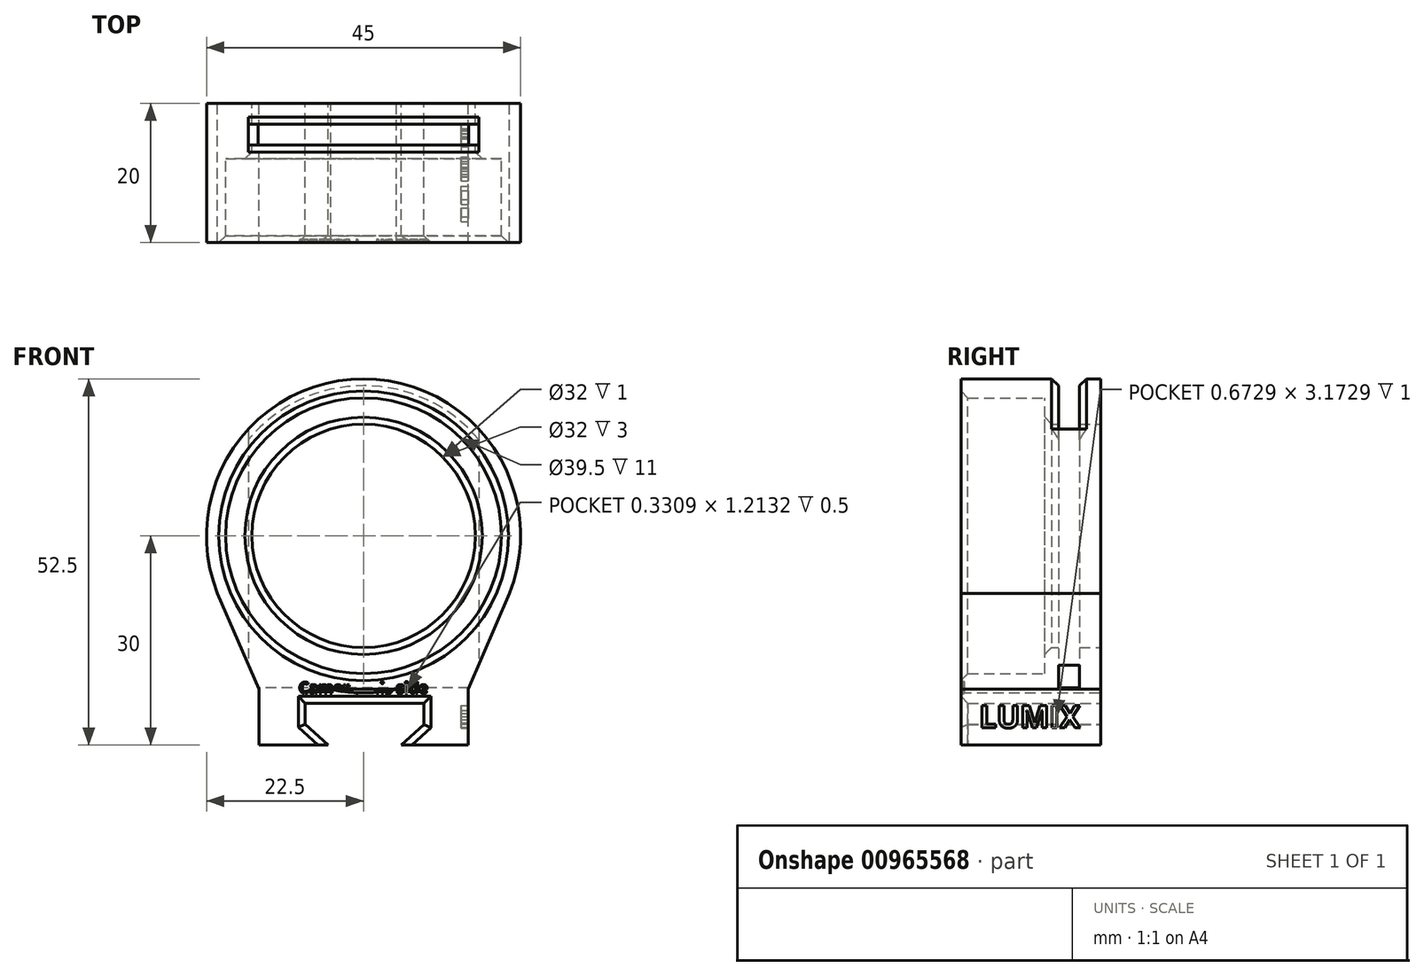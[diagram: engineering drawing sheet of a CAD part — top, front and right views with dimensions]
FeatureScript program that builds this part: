
annotation { "Feature Type Name" : "Feature", "Feature Type Description" : "" }
export const myFeature = defineFeature(function(context is Context, id is Id, definition is map)
    precondition{}
    {
        {
            var Q0;
            Q0=qCreatedBy(makeId("Front.planeOp"),FACE);
            var sketch = newSketch(context, id + "F0", { "sketchPlane" : qUnion([Q0])});
            skLineSegment(sketch, "E0.top", {"start": v(-15, -9.67) * mm, "end": v(15, -9.67) * mm});
            skLineSegment(sketch, "E0.left", {"start": v(-15, -1.67) * mm, "end": v(-15, -9.67) * mm});
            skLineSegment(sketch, "E0.right", {"start": v(15, -1.67) * mm, "end": v(15, -9.67) * mm});
            skLineSegment(sketch, "E1.bottom", {"start": v(-8.57, -3.67) * mm, "end": v(8.93, -3.67) * mm});
            skLineSegment(sketch, "E1.top", {"start": v(-8.57, -9.67) * mm, "end": v(8.93, -9.67) * mm});
            skLineSegment(sketch, "E1.left", {"start": v(-8.57, -3.67) * mm, "end": v(-8.57, -9.67) * mm});
            skLineSegment(sketch, "E1.right", {"start": v(8.93, -3.67) * mm, "end": v(8.93, -9.67) * mm});
            skLineSegment(sketch, "E2.left", {"start": v(-8.57, -9.67) * mm, "end": v(-8.57, -5.78) * mm});
            skLineSegment(sketch, "E3.left", {"start": v(8.93, -9.67) * mm, "end": v(8.93, -5.67) * mm});
            skPoint(sketch, "E4", {"position": v(-8.57, -6.67) * mm});
            skLineSegment(sketch, "E5.bottom", {"start": v(-8.57, -9.67) * mm, "end": v(-9.71, -9.67) * mm, "construction": true});
            skLineSegment(sketch, "E5.top", {"start": v(-8.57, -6.47) * mm, "end": v(-9.71, -6.47) * mm, "construction": true});
            skLineSegment(sketch, "E5.left", {"start": v(-8.57, -9.67) * mm, "end": v(-8.57, -6.47) * mm, "construction": true});
            skLineSegment(sketch, "E5.right", {"start": v(-9.71, -9.67) * mm, "end": v(-9.71, -6.47) * mm, "construction": true});
            skPoint(sketch, "E6.oppositeSnap0", {"position": v(-9.14, -6.47) * mm});
            skLineSegment(sketch, "E6.bottom", {"start": v(8.93, -9.67) * mm, "end": v(10.57, -9.67) * mm, "construction": true});
            skLineSegment(sketch, "E6.top", {"start": v(8.93, -6.47) * mm, "end": v(10.57, -6.47) * mm, "construction": true});
            skLineSegment(sketch, "E6.left", {"start": v(8.93, -9.67) * mm, "end": v(8.93, -6.47) * mm, "construction": true});
            skLineSegment(sketch, "E6.right", {"start": v(10.57, -9.67) * mm, "end": v(10.57, -6.47) * mm, "construction": true});
            skLineSegment(sketch, "E7.bottom", {"start": v(-8.57, -9.67) * mm, "end": v(-5.07, -9.67) * mm, "construction": true});
            skLineSegment(sketch, "E7.top", {"start": v(-8.57, -11.6) * mm, "end": v(-5.07, -11.6) * mm, "construction": true});
            skLineSegment(sketch, "E7.left", {"start": v(-8.57, -9.67) * mm, "end": v(-8.57, -11.6) * mm, "construction": true});
            skLineSegment(sketch, "E7.right", {"start": v(-5.07, -9.67) * mm, "end": v(-5.07, -11.6) * mm, "construction": true});
            skLineSegment(sketch, "E8.bottom", {"start": v(8.93, -9.67) * mm, "end": v(5.43, -9.67) * mm, "construction": true});
            skLineSegment(sketch, "E8.top", {"start": v(8.93, -11.48) * mm, "end": v(5.43, -11.48) * mm, "construction": true});
            skLineSegment(sketch, "E8.left", {"start": v(8.93, -9.67) * mm, "end": v(8.93, -11.48) * mm, "construction": true});
            skLineSegment(sketch, "E8.right", {"start": v(5.43, -9.67) * mm, "end": v(5.43, -11.48) * mm, "construction": true});
            skLineSegment(sketch, "E9", {"start": v(-8.57, -6.47) * mm, "end": v(-5.07, -9.67) * mm});
            skLineSegment(sketch, "E10", {"start": v(5.43, -9.67) * mm, "end": v(8.93, -6.47) * mm});
            skLineSegment(sketch, "E11", {"start": v(-15, -1.67) * mm, "end": v(15, -1.67) * mm});
            skLineSegment(sketch, "E12", {"start": v(0, -1.67) * mm, "end": v(0, 20.33) * mm, "construction": true});
            skCircle(sketch, "E13", {"center": v(0, 20.33) * mm, "radius": 19.75 * mm});
            skCircle(sketch, "E14", {"center": v(0, 20.33) * mm, "radius": 22.5 * mm});
            skLineSegment(sketch, "E15", {"start": v(15, -1.67) * mm, "end": v(20.92, 12.05) * mm});
            skLineSegment(sketch, "E16", {"start": v(-15, -1.67) * mm, "end": v(-20.92, 12.05) * mm});
            skLineSegment(sketch, "E17", {"start": v(15, -4.92) * mm, "end": v(0, -4.92) * mm, "construction": true});
            skLineSegment(sketch, "E18", {"start": v(-15, -4.53) * mm, "end": v(0, -4.53) * mm, "construction": true});
            skLineSegment(sketch, "E19", {"start": v(-8.35, -3.67) * mm, "end": v(-8.35, -6.67) * mm});
            skLineSegment(sketch, "E20", {"start": v(8.67, -3.67) * mm, "end": v(8.67, -6.7) * mm});
            skCircle(sketch, "E21", {"center": v(0, 20.33) * mm, "radius": 16 * mm});
            skSolve(sketch);
        }
        {
            var Q0;
            {var subQ7=sQuery(id+"F0.wireOp",EDGE,"E0.left");Q0=makeQuery(id+"F0.imprint","IMPRINT",FACE,{"disambiguationData":[TD([[makeQuery(id+"F0.imprint","IMPRINT",EDGE,{"derivedFrom":subQ7}),1.0]])]});}
            var Q1;
            {var subQ3=sQuery(id+"F0.wireOp",EDGE,"E9");Q1=makeQuery(id+"F0.imprint","IMPRINT",FACE,{"disambiguationData":[TD([[makeQuery(id+"F0.imprint","IMPRINT",EDGE,{"derivedFrom":subQ3}),-1.0]])]});}
            var Q2;
            {var subQ3=sQuery(id+"F0.wireOp",EDGE,"E10");Q2=makeQuery(id+"F0.imprint","IMPRINT",FACE,{"disambiguationData":[TD([[makeQuery(id+"F0.imprint","IMPRINT",EDGE,{"derivedFrom":subQ3}),-1.0]])]});}
            var Q3;
            Q3=makeQuery(id+"F0.imprint","IMPRINT",FACE,{"disambiguationData":[TD([[makeQuery(id+"F0.imprint","IMPRINT",EDGE,{"derivedFrom":sQuery(id+"F0.wireOp",EDGE,"E13")}),-1.0]])]});
            var Q4;
            {var subQ0=sQuery(id+"F0.wireOp",EDGE,"E14");var subQ1=sQuery(id+"F0.wireOp",EDGE,"E11");var subQ2=makeQuery(id+"F0.imprint","INTERSECT",VERTEX,{"disambiguationData":[OD(0.0)],"derivedFrom":[subQ1,subQ0]});Q4=makeQuery(id+"F0.imprint","IMPRINT",FACE,{"disambiguationData":[TD([[makeQuery(id+"F0.imprint","IMPRINT",EDGE,{"disambiguationData":[TD([[subQ2,-1.0]])],"derivedFrom":subQ1}),-1.0]])]});}
            var Q5;
            {var subQ0=sQuery(id+"F0.wireOp",EDGE,"E16");var subQ3=sQuery(id+"F0.wireOp",EDGE,"E14");var subQ5=makeQuery(id+"F0.imprint","INTERSECT",VERTEX,{"disambiguationData":[OD(1.0)],"derivedFrom":[subQ3,subQ0]});Q5=makeQuery(id+"F0.imprint","IMPRINT",FACE,{"disambiguationData":[TD([[makeQuery(id+"F0.imprint","IMPRINT",EDGE,{"disambiguationData":[TD([[subQ5,-1.0]])],"derivedFrom":subQ3}),-1.0]])]});}
            var Q6;
            {var subQ0=sQuery(id+"F0.wireOp",EDGE,"E15");var subQ3=sQuery(id+"F0.wireOp",EDGE,"E14");var subQ5=makeQuery(id+"F0.imprint","INTERSECT",VERTEX,{"disambiguationData":[OD(1.0)],"derivedFrom":[subQ3,subQ0]});Q6=makeQuery(id+"F0.imprint","IMPRINT",FACE,{"disambiguationData":[TD([[makeQuery(id+"F0.imprint","IMPRINT",EDGE,{"disambiguationData":[TD([[subQ5,1.0]])],"derivedFrom":subQ3}),-1.0]])]});}
            var Q7;
            {var subQ4=sQuery(id+"F0.wireOp",EDGE,"E1.right");Q7=makeQuery(id+"F0.imprint","IMPRINT",FACE,{"disambiguationData":[TD([[makeQuery(id+"F0.imprint","IMPRINT",EDGE,{"derivedFrom":subQ4}),-1.0]])]});}
            var Q8;
            {var subQ4=sQuery(id+"F0.wireOp",EDGE,"E1.left");Q8=makeQuery(id+"F0.imprint","IMPRINT",FACE,{"disambiguationData":[TD([[makeQuery(id+"F0.imprint","IMPRINT",EDGE,{"derivedFrom":subQ4}),1.0]])]});}
            extrude(context, id + "F1", {"entities" : qUnion([Q0, Q1, Q2, Q3, Q4, Q5, Q6, Q7, Q8]), "depth" : 20 * mm, "offsetDistance" : 25 * mm});
        }
        {
            var Q0;
            Q0=qCreatedBy(makeId("Right.planeOp"),FACE);
            var sketch = newSketch(context, id + "F2", { "sketchPlane" : qUnion([Q0])});
            skLineSegment(sketch, "E22.bottom", {"start": v(0, -1.47) * mm, "end": v(-3, -1.47) * mm, "construction": true});
            skLineSegment(sketch, "E22.top", {"start": v(0, 48.53) * mm, "end": v(-3, 48.53) * mm, "construction": true});
            skLineSegment(sketch, "E22.left", {"start": v(0, -1.47) * mm, "end": v(0, 48.53) * mm, "construction": true});
            skLineSegment(sketch, "E22.right", {"start": v(-3, -1.47) * mm, "end": v(-3, 48.53) * mm, "construction": true});
            skLineSegment(sketch, "E23.bottom", {"start": v(-3, 48.53) * mm, "end": v(-6, 48.53) * mm});
            skLineSegment(sketch, "E23.top", {"start": v(-3, -1.47) * mm, "end": v(-6, -1.47) * mm});
            skLineSegment(sketch, "E23.left", {"start": v(-3, 48.53) * mm, "end": v(-3, -1.47) * mm});
            skLineSegment(sketch, "E23.right", {"start": v(-6, 48.53) * mm, "end": v(-6, -1.47) * mm});
            skSolve(sketch);
        }
        {
            var Q0;
            Q0=makeQuery(id+"F0.imprint","IMPRINT",FACE,{"disambiguationData":[TD([[makeQuery(id+"F0.imprint","IMPRINT",EDGE,{"derivedFrom":sQuery(id+"F0.wireOp",EDGE,"E13")}),1.0]])]});
            extrude(context, id + "F3", {"entities" : qUnion([Q0]), "operationType" : NewBodyOperationType.ADD, "depth" : 8 * mm, "offsetDistance" : 25 * mm});
        }
        {
            var Q0;
            Q0=makeQuery(id+"F3.opExtrude","CAP_EDGE",EDGE,{"disambiguationData":[OSD([sQuery(id+"F0.wireOp",EDGE,"E21")])],"isStart":false});
            chamfer(context, id + "F4", {"entities" : qUnion([Q0]), "width" : 1 * mm, "tangentPropagation" : true});
        }
        {
            var Q0;
            Q0=makeQuery(id+"F1.opExtrude","CAP_EDGE",EDGE,{"disambiguationData":[OSD([sQuery(id+"F0.wireOp",EDGE,"E13")])],"isStart":false});
            var Q1;
            Q1=makeQuery(id+"F1.opExtrude","CAP_EDGE",EDGE,{"disambiguationData":[OSD([sQuery(id+"F0.wireOp",EDGE,"E19")])],"isStart":false});
            var Q2;
            Q2=makeQuery(id+"F1.opExtrude","CAP_EDGE",EDGE,{"disambiguationData":[OSD([sQuery(id+"F0.wireOp",EDGE,"E1.bottom")])],"isStart":false});
            var Q3;
            Q3=makeQuery(id+"F1.opExtrude","CAP_EDGE",EDGE,{"disambiguationData":[OSD([sQuery(id+"F0.wireOp",EDGE,"E20")])],"isStart":false});
            var Q4;
            Q4=makeQuery(id+"F1.opExtrude","CAP_EDGE",EDGE,{"disambiguationData":[OSD([sQuery(id+"F0.wireOp",EDGE,"E10")])],"isStart":false});
            var Q5;
            Q5=makeQuery(id+"F1.opExtrude","CAP_EDGE",EDGE,{"disambiguationData":[OSD([sQuery(id+"F0.wireOp",EDGE,"E9")])],"isStart":false});
            chamfer(context, id + "F5", {"entities" : qUnion([Q0, Q1, Q2, Q3, Q4, Q5]), "width" : 1 * mm, "tangentPropagation" : true});
        }
        {
            var Q0;
            Q0=makeQuery(id+"F2.imprint","IMPRINT",FACE,{"disambiguationData":[TD([[makeQuery(id+"F2.imprint","IMPRINT",EDGE,{"derivedFrom":sQuery(id+"F2.wireOp",EDGE,"E23.bottom")}),1.0]])]});
            extrude(context, id + "F6", {"entities" : qUnion([Q0]), "operationType" : NewBodyOperationType.REMOVE, "depth" : 33 * mm, "offsetDistance" : 25 * mm, "symmetric" : true});
        }
        {
            var Q0;
            Q0=makeQuery(id+"F6.boolean.opBoolean","INTERSECT",EDGE,{"derivedFrom":[makeQuery(id+"F1.opExtrude","SWEPT_FACE",FACE,{"disambiguationData":[OSD([sQuery(id+"F0.wireOp",EDGE,"E14")])]}),makeQuery(id+"F6.opExtrude","SWEPT_FACE",FACE,{"disambiguationData":[OSD([sQuery(id+"F2.wireOp",EDGE,"E23.right")])]})]});
            var Q1;
            Q1=makeQuery(id+"F6.boolean.opBoolean","INTERSECT",EDGE,{"derivedFrom":[makeQuery(id+"F1.opExtrude","SWEPT_FACE",FACE,{"disambiguationData":[OSD([sQuery(id+"F0.wireOp",EDGE,"E14")])]}),makeQuery(id+"F6.opExtrude","SWEPT_FACE",FACE,{"disambiguationData":[OSD([sQuery(id+"F2.wireOp",EDGE,"E23.left")])]})]});
            chamfer(context, id + "F7", {"entities" : qUnion([Q0, Q1]), "width" : 1 * mm, "tangentPropagation" : true});
        }
        {
            var Q0;
            Q0=makeQuery(id+"F1.opExtrude","SWEPT_FACE",FACE,{"disambiguationData":[OSD([sQuery(id+"F0.wireOp",EDGE,"E0.right")])]});
            var sketch = newSketch(context, id + "F8", { "sketchPlane" : qUnion([Q0])});
            skText(sketch, "E24", { "text": "LUMIX", "fontName": "OpenSans-Bold.ttf"});
            const initialGuessF8  = {"E24": [-0.01739, -0.0072, 1, 0, 0.0032]};
            skSetInitialGuess(sketch, initialGuessF8);
            skSolve(sketch);
        }
        {
            var Q0;
            Q0=makeQuery(id+"F8.imprint","IMPRINT",FACE,{"disambiguationData":[TD([[makeQuery(id+"F8.imprint","IMPRINT",EDGE,{"derivedFrom":sQuery(id+"F8.wireOp",EDGE,"E24.sketch_text.stroke-0")}),-1.0]])]});
            var Q1;
            Q1=makeQuery(id+"F8.imprint","IMPRINT",FACE,{"disambiguationData":[TD([[makeQuery(id+"F8.imprint","IMPRINT",EDGE,{"derivedFrom":sQuery(id+"F8.wireOp",EDGE,"E24.sketch_text.stroke-6")}),-1.0]])]});
            var Q2;
            Q2=makeQuery(id+"F8.imprint","IMPRINT",FACE,{"disambiguationData":[TD([[makeQuery(id+"F8.imprint","IMPRINT",EDGE,{"derivedFrom":sQuery(id+"F8.wireOp",EDGE,"E24.sketch_text.stroke-21")}),-1.0]])]});
            var Q3;
            Q3=makeQuery(id+"F8.imprint","IMPRINT",FACE,{"disambiguationData":[TD([[makeQuery(id+"F8.imprint","IMPRINT",EDGE,{"derivedFrom":sQuery(id+"F8.wireOp",EDGE,"E24.sketch_text.stroke-40")}),-1.0]])]});
            var Q4;
            Q4=makeQuery(id+"F8.imprint","IMPRINT",FACE,{"disambiguationData":[TD([[makeQuery(id+"F8.imprint","IMPRINT",EDGE,{"derivedFrom":sQuery(id+"F8.wireOp",EDGE,"E24.sketch_text.stroke-44")}),-1.0]])]});
            extrude(context, id + "F9", {"entities" : qUnion([Q0, Q1, Q2, Q3, Q4]), "operationType" : NewBodyOperationType.REMOVE, "oppositeDirection" : true, "depth" : 1 * mm, "offsetDistance" : 25 * mm});
        }
        {
            var Q0;
            Q0=makeQuery(id+"F1.opExtrude","CAP_FACE",FACE,{"disambiguationData":[OSD([sQuery(id+"F0.wireOp",EDGE,"E0.top"),sQuery(id+"F0.wireOp",EDGE,"E0.left"),sQuery(id+"F0.wireOp",EDGE,"E0.right"),sQuery(id+"F0.wireOp",EDGE,"E1.bottom"),sQuery(id+"F0.wireOp",EDGE,"E1.top"),sQuery(id+"F0.wireOp",EDGE,"E9"),sQuery(id+"F0.wireOp",EDGE,"E10"),sQuery(id+"F0.wireOp",EDGE,"E13"),sQuery(id+"F0.wireOp",EDGE,"E14"),sQuery(id+"F0.wireOp",EDGE,"E15"),sQuery(id+"F0.wireOp",EDGE,"E16"),sQuery(id+"F0.wireOp",EDGE,"E19"),sQuery(id+"F0.wireOp",EDGE,"E20")])],"isStart":false});
            var sketch = newSketch(context, id + "F10", { "sketchPlane" : qUnion([Q0])});
            skText(sketch, "E25", { "text": "Camera this side", "fontName": "OpenSans-Bold.ttf"});
            const initialGuessF10  = {"E25": [-0.00926, -0.00223, 1, 0, 0.0016]};
            skSetInitialGuess(sketch, initialGuessF10);
            skSolve(sketch);
        }
        {
            var Q0;
            Q0=makeQuery(id+"F10.imprint","IMPRINT",FACE,{"disambiguationData":[TD([[makeQuery(id+"F10.imprint","IMPRINT",EDGE,{"derivedFrom":sQuery(id+"F10.wireOp",EDGE,"E25.sketch_text.stroke-0")}),-1.0]])]});
            var Q1;
            Q1=makeQuery(id+"F10.imprint","IMPRINT",FACE,{"disambiguationData":[TD([[makeQuery(id+"F10.imprint","IMPRINT",EDGE,{"derivedFrom":sQuery(id+"F10.wireOp",EDGE,"E25.sketch_text.stroke-15")}),-1.0]])]});
            var Q2;
            Q2=makeQuery(id+"F10.imprint","IMPRINT",FACE,{"disambiguationData":[TD([[makeQuery(id+"F10.imprint","IMPRINT",EDGE,{"derivedFrom":sQuery(id+"F10.wireOp",EDGE,"E25.sketch_text.stroke-40")}),-1.0]])]});
            var Q3;
            Q3=makeQuery(id+"F10.imprint","IMPRINT",FACE,{"disambiguationData":[TD([[makeQuery(id+"F10.imprint","IMPRINT",EDGE,{"derivedFrom":sQuery(id+"F10.wireOp",EDGE,"E25.sketch_text.stroke-68")}),-1.0]])]});
            var Q4;
            Q4=makeQuery(id+"F10.imprint","IMPRINT",FACE,{"disambiguationData":[TD([[makeQuery(id+"F10.imprint","IMPRINT",EDGE,{"derivedFrom":sQuery(id+"F10.wireOp",EDGE,"E25.sketch_text.stroke-88")}),-1.0]])]});
            var Q5;
            Q5=makeQuery(id+"F10.imprint","IMPRINT",FACE,{"disambiguationData":[TD([[makeQuery(id+"F10.imprint","IMPRINT",EDGE,{"derivedFrom":sQuery(id+"F10.wireOp",EDGE,"E25.sketch_text.stroke-101")}),-1.0]])]});
            var Q6;
            Q6=makeQuery(id+"F10.imprint","IMPRINT",FACE,{"disambiguationData":[TD([[makeQuery(id+"F10.imprint","IMPRINT",EDGE,{"derivedFrom":sQuery(id+"F10.wireOp",EDGE,"E25.sketch_text.stroke-126")}),-1.0]])]});
            var Q7;
            Q7=makeQuery(id+"F10.imprint","IMPRINT",FACE,{"disambiguationData":[TD([[makeQuery(id+"F10.imprint","IMPRINT",EDGE,{"derivedFrom":sQuery(id+"F10.wireOp",EDGE,"E25.sketch_text.stroke-144")}),-1.0]])]});
            var Q8;
            Q8=makeQuery(id+"F10.imprint","IMPRINT",FACE,{"disambiguationData":[TD([[makeQuery(id+"F10.imprint","IMPRINT",EDGE,{"derivedFrom":sQuery(id+"F10.wireOp",EDGE,"E25.sketch_text.stroke-166")}),-1.0]])]});
            var Q9;
            Q9=makeQuery(id+"F10.imprint","IMPRINT",FACE,{"disambiguationData":[TD([[makeQuery(id+"F10.imprint","IMPRINT",EDGE,{"derivedFrom":sQuery(id+"F10.wireOp",EDGE,"E25.sketch_text.stroke-161")}),-1.0]])]});
            var Q10;
            Q10=makeQuery(id+"F10.imprint","IMPRINT",FACE,{"disambiguationData":[TD([[makeQuery(id+"F10.imprint","IMPRINT",EDGE,{"derivedFrom":sQuery(id+"F10.wireOp",EDGE,"E25.sketch_text.stroke-170")}),-1.0]])]});
            var Q11;
            Q11=makeQuery(id+"F10.imprint","IMPRINT",FACE,{"disambiguationData":[TD([[makeQuery(id+"F10.imprint","IMPRINT",EDGE,{"derivedFrom":sQuery(id+"F10.wireOp",EDGE,"E25.sketch_text.stroke-222")}),-1.0]])]});
            var Q12;
            Q12=makeQuery(id+"F10.imprint","IMPRINT",FACE,{"disambiguationData":[TD([[makeQuery(id+"F10.imprint","IMPRINT",EDGE,{"derivedFrom":sQuery(id+"F10.wireOp",EDGE,"E25.sketch_text.stroke-196")}),-1.0]])]});
            var Q13;
            Q13=makeQuery(id+"F10.imprint","IMPRINT",FACE,{"disambiguationData":[TD([[makeQuery(id+"F10.imprint","IMPRINT",EDGE,{"derivedFrom":sQuery(id+"F10.wireOp",EDGE,"E25.sketch_text.stroke-227")}),-1.0]])]});
            var Q14;
            Q14=makeQuery(id+"F10.imprint","IMPRINT",FACE,{"disambiguationData":[TD([[makeQuery(id+"F10.imprint","IMPRINT",EDGE,{"derivedFrom":sQuery(id+"F10.wireOp",EDGE,"E25.sketch_text.stroke-231")}),-1.0]])]});
            var Q15;
            Q15=makeQuery(id+"F10.imprint","IMPRINT",FACE,{"disambiguationData":[TD([[makeQuery(id+"F10.imprint","IMPRINT",EDGE,{"derivedFrom":sQuery(id+"F10.wireOp",EDGE,"E25.sketch_text.stroke-254")}),-1.0]])]});
            extrude(context, id + "F11", {"entities" : qUnion([Q0, Q1, Q2, Q3, Q4, Q5, Q6, Q7, Q8, Q9, Q10, Q11, Q12, Q13, Q14, Q15]), "operationType" : NewBodyOperationType.REMOVE, "oppositeDirection" : true, "depth" : 0.5 * mm, "offsetDistance" : 25 * mm});
        }
    });
